# Revit family: Factory Light 6 Rod Pendant
name_source: partatom
category: Lighting Fixtures
revit_build: Autodesk Revit 2017 (Build: 20181011_1645(x64)
units: mm (PartAtom-declared; Revit-internal decimal feet)

## family parameters
Cut with Voids When Loaded = No
Host = Face
Light Source = Yes
Part Type = Normal
Room Calculation Point = No
Round Connector Dimension = Use Diameter
Shared = No

## types (1)
- White w/ Cage
    Cage Height = -0' - 0 1/2"
    Cage Visibility = Yes
    Canopy Width = 0' - 4 3/4"
    Color Filter = 16777215
    Cost = 389 $
    Default Elevation = 4' - 0"
    Description = Industrial and utilitarian, the Factory Light 6 Rod Pendant is a perfect example of traditional factory-style lighting made popular in the 1930's. Curved bell shape allows for excellent task lighting, and top cutouts add a sleek design element with the added function of releasing excess heat. Made from powder coated, hand-spun steel and produced on an RLM tool made exclusively for Schoolhouse. Manufactured in our Portland, Ore. factory to exacting specifications. A Schoolhouse Original.
    Dimming Lamp Color Temperature Shift = <None>
    Height = 2' - 10"
    Length = 1' - 0"
    Light Source Symbol Length = 5' - 0"
    Manufacturer = Schoolhouse
    Max Wattage = 150 W
    Model = Factory Light 6 Rod Pendant
    Primary Finishes = Schoolhouse White 255-255-255
    Product Material = Steel
    Spot Beam Angle = 30.00°
    Spot Field Angle = 70.00°
    Tilt Angle = 90.00°
    URL = https://www.schoolhouse.com
    Voltage = 120V

## geometry (parser evidence)
native form markers: Sweep x4
no freeform markers — native parametric forms only
